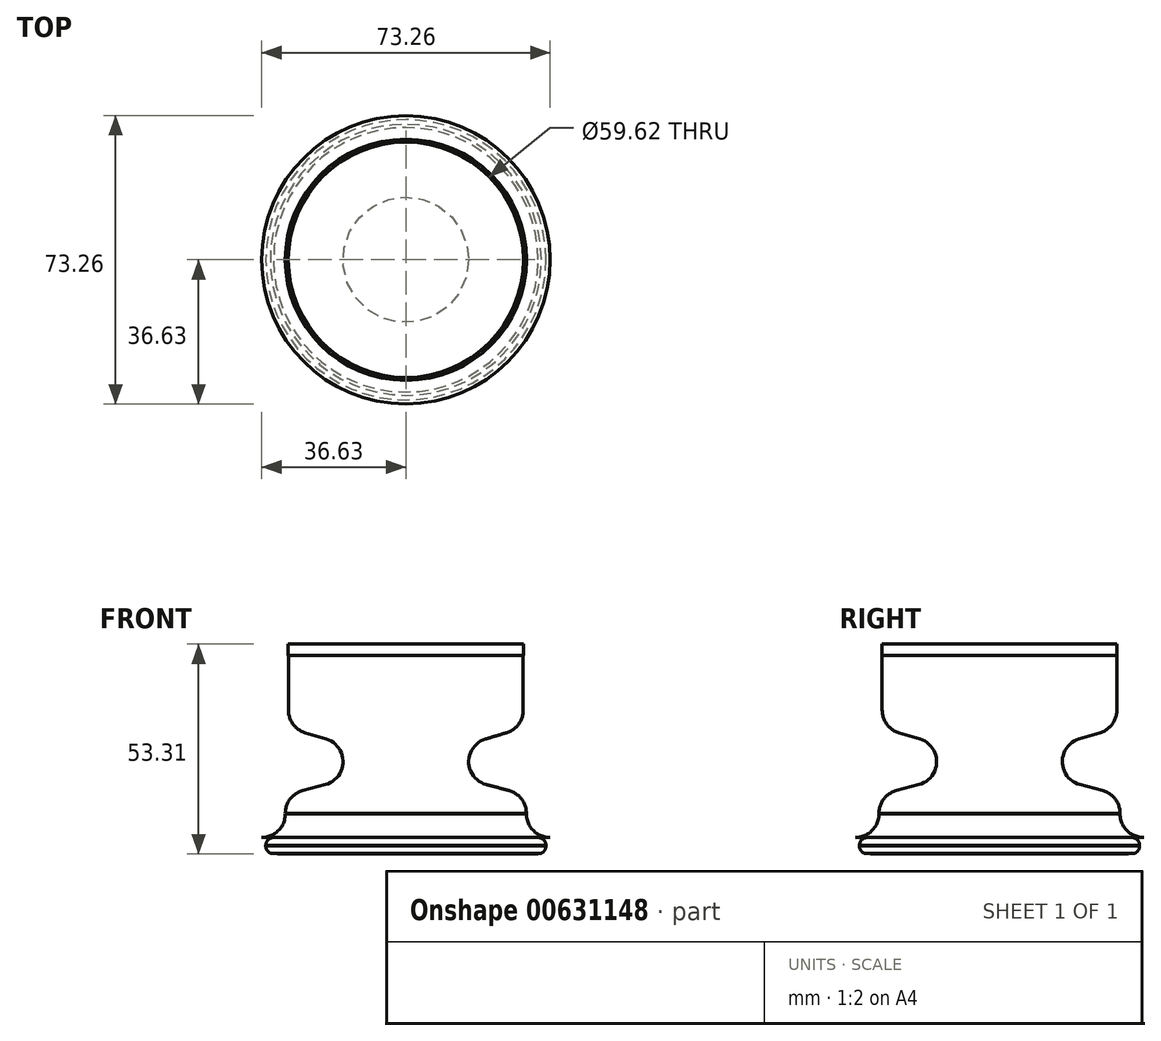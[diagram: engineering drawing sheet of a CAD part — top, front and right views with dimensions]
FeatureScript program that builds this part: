
annotation { "Feature Type Name" : "Feature", "Feature Type Description" : "" }
export const myFeature = defineFeature(function(context is Context, id is Id, definition is map)
    precondition{}
    {
        {
            var Q0;
            Q0=qCreatedBy(makeId("Front.planeOp"),FACE);
            var sketch = newSketch(context, id + "F0", { "sketchPlane" : qUnion([Q0])});
            skLineSegment(sketch, "E0", {"start": v(0, 0) * mm, "end": v(33.6, 0) * mm});
            skLineSegment(sketch, "E1", {"start": v(35.6, 2) * mm, "end": v(35.6, 2.16) * mm});
            skLineSegment(sketch, "E2", {"start": v(36.63, 4.16) * mm, "end": v(33.6, 4.16) * mm});
            skLineSegment(sketch, "E3", {"start": v(30.63, 10.16) * mm, "end": v(30.63, 10.3) * mm});
            skLineSegment(sketch, "E4", {"start": v(26.17, 16.1) * mm, "end": v(20.42, 17.63) * mm});
            skLineSegment(sketch, "E5", {"start": v(20.23, 29.17) * mm, "end": v(25.54, 30.77) * mm});
            skLineSegment(sketch, "E6", {"start": v(29.81, 36.52) * mm, "end": v(29.81, 50.43) * mm});
            skPoint(sketch, "E7.visualSharp", {"position": v(35.6, 0) * mm});
            skArc(sketch, "E7.filletArc", {"start": v(34.42, 0.18) * mm, "mid": v(35.27, 0.92) * mm, "end": v(35.6, 2) * mm});
            skPoint(sketch, "E8.visualSharp", {"position": v(33.6, 0) * mm});
            skArc(sketch, "E8.filletArc", {"start": v(33.6, 0) * mm, "mid": v(34.02, 0.05) * mm, "end": v(34.42, 0.18) * mm});
            skPoint(sketch, "E9.visualSharp", {"position": v(35.6, 4.16) * mm});
            skArc(sketch, "E9.filletArc", {"start": v(35.6, 2.16) * mm, "mid": v(35, 3.58) * mm, "end": v(33.6, 4.16) * mm});
            skPoint(sketch, "E10.visualSharp", {"position": v(30.63, 4.16) * mm});
            skArc(sketch, "E10.filletArc", {"start": v(30.63, 10.16) * mm, "mid": v(32.39, 5.92) * mm, "end": v(36.63, 4.16) * mm});
            skPoint(sketch, "E11.visualSharp", {"position": v(30.63, 14.9) * mm});
            skArc(sketch, "E11.filletArc", {"start": v(30.63, 10.3) * mm, "mid": v(29.39, 13.95) * mm, "end": v(26.17, 16.1) * mm});
            skPoint(sketch, "E12.visualSharp", {"position": v(0, 23.07) * mm});
            skArc(sketch, "E12.filletArc", {"start": v(20.23, 29.17) * mm, "mid": v(15.96, 23.33) * mm, "end": v(20.42, 17.63) * mm});
            skPoint(sketch, "E13.visualSharp", {"position": v(29.81, 32.06) * mm});
            skArc(sketch, "E13.filletArc", {"start": v(25.54, 30.77) * mm, "mid": v(28.63, 32.94) * mm, "end": v(29.81, 36.52) * mm});
            skSolve(sketch);
        }
        {
            var Q0;
            Q0=qCreatedBy(makeId("Front.planeOp"),FACE);
            var sketch = newSketch(context, id + "F1", { "sketchPlane" : qUnion([Q0])});
            skLineSegment(sketch, "E14", {"start": v(0, 0) * mm, "end": v(0, 53.3) * mm, "construction": true});
            skLineSegment(sketch, "E15", {"start": v(0, 53.3) * mm, "end": v(29.88, 53.3) * mm});
            skLineSegment(sketch, "E16", {"start": v(29.88, 53.3) * mm, "end": v(29.88, 50.43) * mm});
            skSolve(sketch);
        }
        {
            var Q0;
            Q0=sQuery(id+"F0.wireOp",EDGE,"E0");
            var Q1;
            Q1=sQuery(id+"F0.wireOp",EDGE,"E7.filletArc");
            var Q2;
            Q2=sQuery(id+"F0.wireOp",EDGE,"E9.filletArc");
            var Q3;
            Q3=sQuery(id+"F0.wireOp",EDGE,"E10.filletArc");
            var Q4;
            Q4=sQuery(id+"F0.wireOp",EDGE,"E11.filletArc");
            var Q5;
            Q5=sQuery(id+"F0.wireOp",EDGE,"E4");
            var Q6;
            Q6=sQuery(id+"F0.wireOp",EDGE,"E12.filletArc");
            var Q7;
            Q7=sQuery(id+"F0.wireOp",EDGE,"E5");
            var Q8;
            Q8=sQuery(id+"F0.wireOp",EDGE,"E13.filletArc");
            var Q9;
            Q9=sQuery(id+"F0.wireOp",EDGE,"E6");
            var Q10;
            Q10=sQuery(id+"F1.wireOp",EDGE,"E16");
            var Q11;
            Q11=sQuery(id+"F1.wireOp",EDGE,"E15");
            var Q12;
            Q12=sQuery(id+"F1.wireOp",EDGE,"E14");
            revolve(context, id + "F2", {"bodyType" : ToolBodyType.SURFACE, "surfaceEntities" : qUnion([Q0, Q1, Q2, Q3, Q4, Q5, Q6, Q7, Q8, Q9, Q10, Q11]), "axis" : qUnion([Q12]), "revolveType" : RevolveType.FULL});
        }
    });
